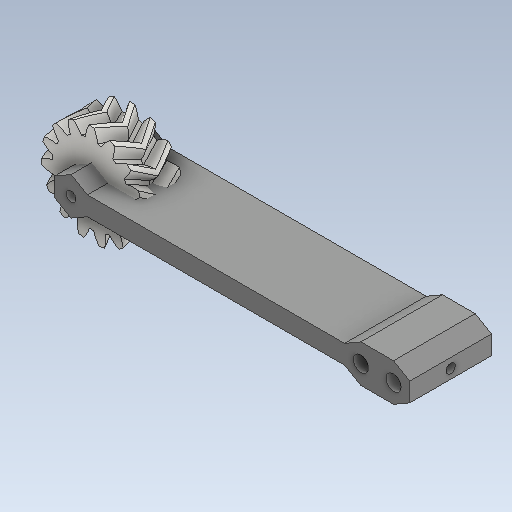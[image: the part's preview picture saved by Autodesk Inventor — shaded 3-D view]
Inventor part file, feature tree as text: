
AUTODESK INVENTOR PART (.ipt)
format: ipt  version: 2020 (Build 240168000, 168)  size: 981,504 bytes
history: native  units: in
note: dims shown in document units (in); Inventor stores cm internally (conversion verified against a paired STEP export)
features: sketch x5, extrude x4, other x3, plane x2, mirror x1, projected_geometry x1
ambient origin geometry x8: Origin, YZ Plane, XZ Plane, XY Plane, X Axis, Y Axis, Z Axis, Center Point
bodies: Solid1 (feature_tree), Solid2 (feature_tree)
feature tree (16):
  other  "Spur Gear1"
  plane  "Work Plane3"
  extrude  "Extrusion1"  Depth=3.4256in
  plane  "Work Plane1"
  extrude  "Extrusion2"  Depth=0.7874in
  sketch  "Sketch4"  dims[d4=0.0in d5=0.0906in]
  extrude  "Extrusion4"  Depth=0.0906in
  mirror  "Mirror3"
  extrude  "Extrusion11"  Depth=0.315in
  sketch  "Sketch1"  dims[d0=0.1818in d1=3.4256in]
  sketch  "Sketch2"  dims[d2=0.0945in d3=0.7874in]
  sketch  "Sketch5"  dims[d6=0.7874in d7=0.0in d29=0.315in]
  other  "Solid1::Spur Gear1"
  other  "TaggingFeature1"
  projected_geometry  "Projected Loop11"
  sketch  "Sketch15"  dims[d31=0.315in d33=0.1476in d34=0.2362in d35=0.0in d38=0.315in d69=2.4807in d70=0.3937in d71=0.1969in d79=0.0in d80=0.3937in d81=0.0in]
